# Revit family: 63_LF_UN_Zumtobel Ondaria_IVLB
name_source: partatom
category: Lighting Fixtures
revit_build: Autodesk Revit 2017 (Build: 20190508_0315(x64)
units: mm (PartAtom-declared; Revit-internal decimal feet)

## family parameters
Always vertical = No
Cut with Voids When Loaded = No
Light Source = No
Part Type = Normal
Room Calculation Point = No
Round Connector Dimension = Use Diameter
Shared = No
Work Plane-Based = No

## types (1)
- Costumizable - Family Instance
    Apparent Load = 0 VA
    Assembly Code = 63.0
    Calc_Recessed = 87 mm  [stored 0.285433 ft]
    Description = Geometry copy of fixture
    Family Instance = Zumtobel ONDARIA 2 : ONDARIA 2 D400 LED
    IfcExportAs = IfcLightFixtureType
    IfcExportType = USERDEFINED
    Model = Generic Geometry
    Recessed = Yes
    Rotation XZ Axis = 0.00°
    Rotation YZ Axis = 0.00°
    Suspension = No
    Type Comments = Unhosted - IVLibrary

note: [stored X ft] marks values corroborated as IEEE doubles in the binary element streams (Revit-internal decimal feet)

## geometry (parser evidence)
native form markers: Blend x18, Sweep x12
no freeform markers — native parametric forms only
